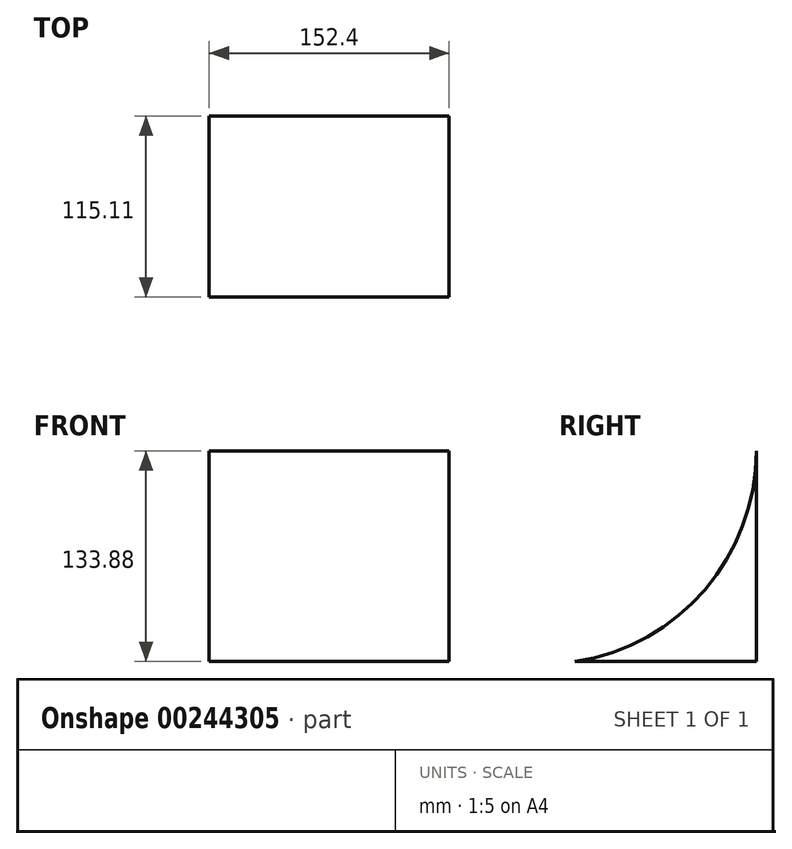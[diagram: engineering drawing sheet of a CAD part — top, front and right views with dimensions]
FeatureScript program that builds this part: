
annotation { "Feature Type Name" : "Feature", "Feature Type Description" : "" }
export const myFeature = defineFeature(function(context is Context, id is Id, definition is map)
    precondition{}
    {
        {
            var Q0;
            Q0=qCreatedBy(makeId("Right.planeOp"),FACE);
            var sketch = newSketch(context, id + "F0", { "sketchPlane" : qUnion([Q0])});
            skLineSegment(sketch, "E0", {"start": v(-127.63, 0) * mm, "end": v(-127.63, 132.63) * mm});
            skLineSegment(sketch, "E1", {"start": v(-127.63, 132.63) * mm, "end": v(-127.63, 0) * mm});
            skLineSegment(sketch, "E2", {"start": v(-127.63, 0) * mm, "end": v(126.37, 0) * mm});
            skLineSegment(sketch, "E3", {"start": v(126.37, 0) * mm, "end": v(126.37, 133.88) * mm});
            skArc(sketch, "E4", {"start": v(11.26, 0) * mm, "mid": v(93.64, 45.6) * mm, "end": v(126.37, 133.88) * mm});
            skArc(sketch, "E5", {"start": v(-127.63, 132.63) * mm, "mid": v(-90.54, 40.6) * mm, "end": v(0, 0) * mm});
            skSolve(sketch);
        }
        {
            var Q0;
            {var subQ0=sQuery(id+"F0.wireOp",EDGE,"E3");Q0=makeQuery(id+"F0.imprint","IMPRINT",FACE,{"disambiguationData":[TD([[makeQuery(id+"F0.imprint","IMPRINT",EDGE,{"derivedFrom":subQ0}),1.0]])]});}
            var Q1;
            {var subQ0=sQuery(id+"F0.wireOp",EDGE,"E1");Q1=makeQuery(id+"F0.imprint","IMPRINT",FACE,{"disambiguationData":[TD([[makeQuery(id+"F0.imprint","IMPRINT",EDGE,{"derivedFrom":subQ0}),1.0]])]});}
            extrude(context, id + "F1", {"entities" : qUnion([Q0, Q1]), "depth" : 152.4 * mm});
        }
    });
